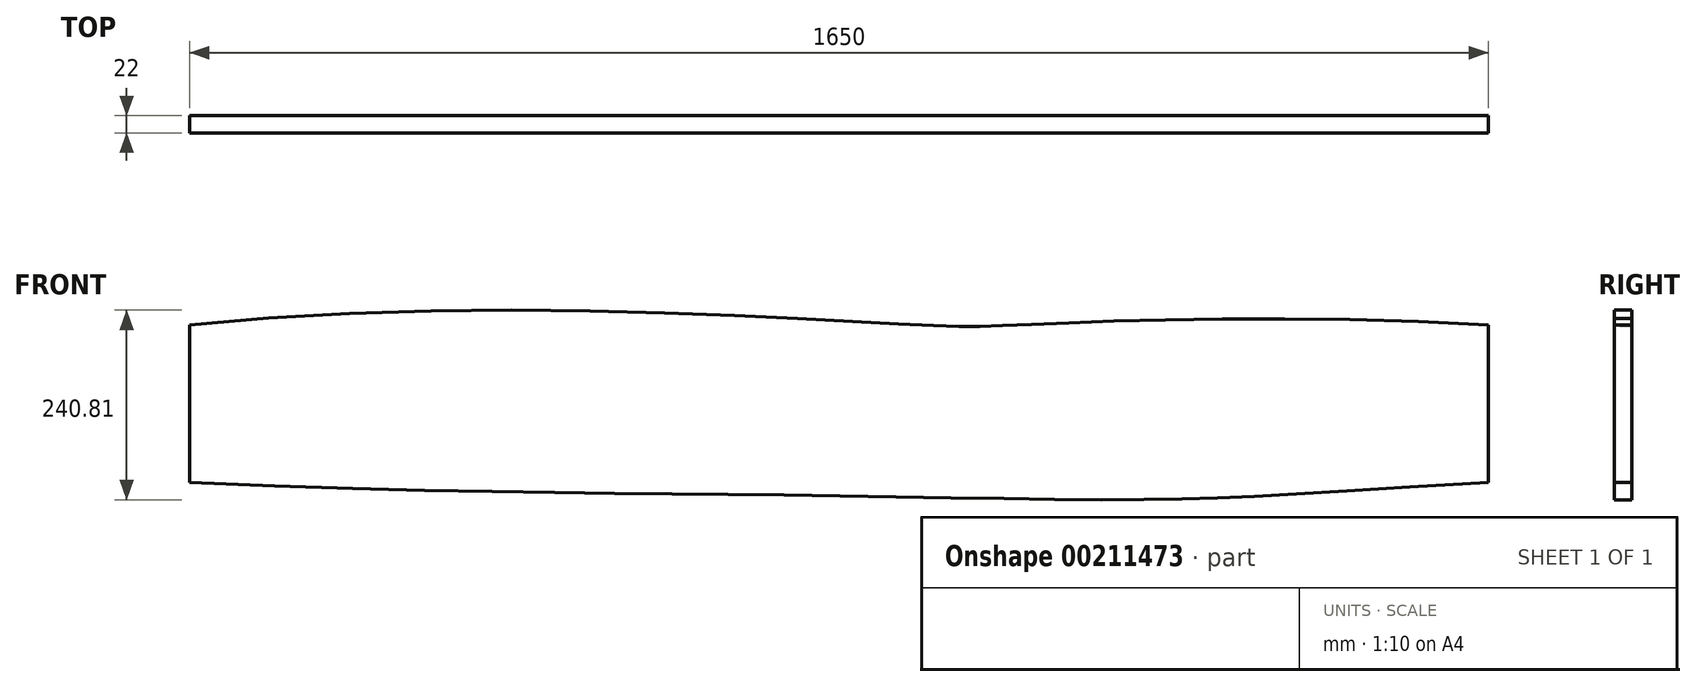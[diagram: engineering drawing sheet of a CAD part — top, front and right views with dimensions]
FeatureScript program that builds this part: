
annotation { "Feature Type Name" : "Feature", "Feature Type Description" : "" }
export const myFeature = defineFeature(function(context is Context, id is Id, definition is map)
    precondition{}
    {
        {
            var Q0;
            Q0=qCreatedBy(makeId("Front.planeOp"),FACE);
            var sketch = newSketch(context, id + "F0", { "sketchPlane" : qUnion([Q0])});
            skLineSegment(sketch, "E0.bottom", {"start": v(853.02, 100) * mm, "end": v(-796.98, 100) * mm, "construction": true});
            skLineSegment(sketch, "E0.top", {"start": v(853.02, -100) * mm, "end": v(-796.98, -100) * mm, "construction": true});
            skLineSegment(sketch, "E0.left", {"start": v(853.02, 100) * mm, "end": v(853.02, -100) * mm, "construction": true});
            skLineSegment(sketch, "E0.right", {"start": v(-796.98, 100) * mm, "end": v(-796.98, -100) * mm, "construction": true});
            skPoint(sketch, "E0.middle", {"position": v(28.02, 0) * mm});
            skLineSegment(sketch, "E1", {"start": v(-796.98, 100) * mm, "end": v(-796.98, -100) * mm});
            skLineSegment(sketch, "E2", {"start": v(853.02, 100) * mm, "end": v(853.02, -100) * mm});
            skFitSpline(sketch, "E3", {"points": [v(-796.98, 100) * mm, v(134.63, 100) * mm, v(249.63, 100) * mm, v(853.02, 100) * mm], "startDerivative": vector(2262.87, 251.46) * mm, "endDerivative": vector(2066.33, -127.25) * mm});
            skFitSpline(sketch, "E4", {"points": [v(-796.98, -100) * mm, v(-34.93, -115.95) * mm, v(423.62, -121.69) * mm, v(853.02, -100) * mm], "startDerivative": vector(2594.1, -107.22) * mm, "endDerivative": vector(2571.13, 143.98) * mm});
            skSolve(sketch);
        }
        {
            var Q0;
            Q0=qSketchRegion(id+"F0",true);
            extrude(context, id + "F1", {"entities" : qUnion([Q0]), "depth" : 22 * mm});
        }
    });
